# Revit family: Domotics-DomesticRanges-GEWISS-SYSTEM_PROTECTION-ONE-WAY_SWITCH_RCBO
name_source: partatom
category: Apparecchi elettrici
revit_build: Autodesk Revit 2016 (Build: 20161004_0715(x64)
units: mm (PartAtom-declared; Revit-internal decimal feet)

## family parameters
Condiviso = Sì
Host = Superficie
Mantenere orientamento annotazione = Sì
Punto di calcolo locali = Sì
Quota connettore circolare = Usa diametro
Taglio con vuoti quando caricato = No
Tipo di parte = Normale

## types (12) — shared parameters
Breaking capacity = 3KA
Carico apparente = 0 VA
Catalogue = DOMOTICS
Catalogue Range = SYSTEM - DOMESTIC RANGE
Curve = C
Description. = One-way switch (1P+N)
Description: = Two-pole (1P+N)
Electrocod = 0131
IDF = 34736507-47ea-4ef1-b0f9-27655b7c507a
IDT = 7dbccad0-54d6-49f8-8b47-8e5b81d17638
Immagine tipo = GW21450.jpg
N. poli = 1
No. SYSTEM modules = 2
Produttore = GEWISS S.p.A.
Prospetto di default = 1219 mm
SEO = RCCB
TIPO = System Int Magnetot.Differenziale_GENERICO : NERO
Technical sheet = https://www.gewiss.com
Type = Miniature circuit breaker + residual current device
Type: = A
URL = https://www.gewiss.com
Version file RFA = 19.4
Volt = 230 V
Voltage = 230V ac
Voltage: = 230V ac

## per-type parameters (varying)
| type | Colour | Descrizione | EAN code | Idn | Modello | Rated current (A) | Rated current (In) | Rated residual operating current |
| GW20450 - RCBO-1P+N C16 idn 30ma 230V 3kA white | White | RCBO-1P+N C16 IDN 30MA 230V 3KA SY/WT | 8011564113022 | 30MA | GW20450 | 16 | 16 | 30MA |
| GW21449 - RCBO-1P+N C10 idn 30ma 230V 3kA black | Black | RCBO-1P+N C10 IDN 30MA 230V 3KA SY/BK | 8011564129245 | 30MA | GW21449 | 10 | 10 | 30MA |
| GW21448 - RCBO-1P+N C6 idn 30ma 230V 3kA black | Black | RCBO-1P+N C6 IDN 30MA 230V 3KA SY/BK | 8011564129238 | 30MA | GW21448 | 6 | 6 | 30MA |
| GW20437 - RCBO-1P+N C6 idn 10ma 230V 3kA white | White | RCBO-1P+N C6 IDN 10MA 230V 3KA SY/WT | 8011564079694 | 10MA | GW20437 | 6 | 6 | 10MA |
| GW20449 - RCBO-1P+N C10 idn 30ma 230V 3kA white | White | RCBO-1P+N C10 IDN 30MA 230V 3KA SY/WT | 8011564113015 | 30MA | GW20449 | 10 | 10 | 30MA |
| GW20448 - RCBO-1P+N C6 idn 30ma 230V 3kA white | White | RCBO-1P+N C6 IDN 30MA 230V 3KA SY/WT | 8011564113008 | 30MA | GW20448 | 6 | 6 | 30MA |
| GW20439 - RCBO-1P+N C16 idn 10ma 230V 3kA white | White | RCBO-1P+N C16 IDN 10MA 230V 3KA SY/WT | 8011564079717 | 10MA | GW20439 | 16 | 16 | 10MA |
| GW21438 - RCBO-1P+N C10 idn 10ma 230V 3kA black | Black | RCBO-1P+N C10 IDN 10MA 230V 3KA SY/BK | 8011564129214 | 10MA | GW21438 | 10 | 10 | 10MA |
| GW21450 - RCBO-1P+N C16 idn 30ma 230V 3kA black | Black | RCBO-1P+N C16 IDN 30MA 230V 3KA SY/BK | 8011564129252 | 30MA | GW21450 | 16 | 16 | 30MA |
| GW21439 - RCBO-1P+N C16 idn 10ma 230V 3kA black | Black | RCBO-1P+N C16 IDN 10MA 230V 3KA SY/BK | 8011564129221 | 10MA | GW21439 | 16 | 16 | 10MA |
| GW20438 - RCBO-1P+N C10 idn 10ma 230V 3kA white | White | RCBO-1P+N C10 IDN 10MA 230V 3KA SY/WT | 8011564079700 | 10MA | GW20438 | 10 | 10 | 10MA |
| GW21437 - RCBO-1P+N C6 idn 10ma 230V 3kA black | Black | RCBO-1P+N C6 IDN 10MA 230V 3KA SY/BK | 8011564129207 | 10MA | GW21437 | 6 | 6 | 10MA |

## geometry (parser evidence)
native form markers: Sweep x2
no freeform markers — native parametric forms only
